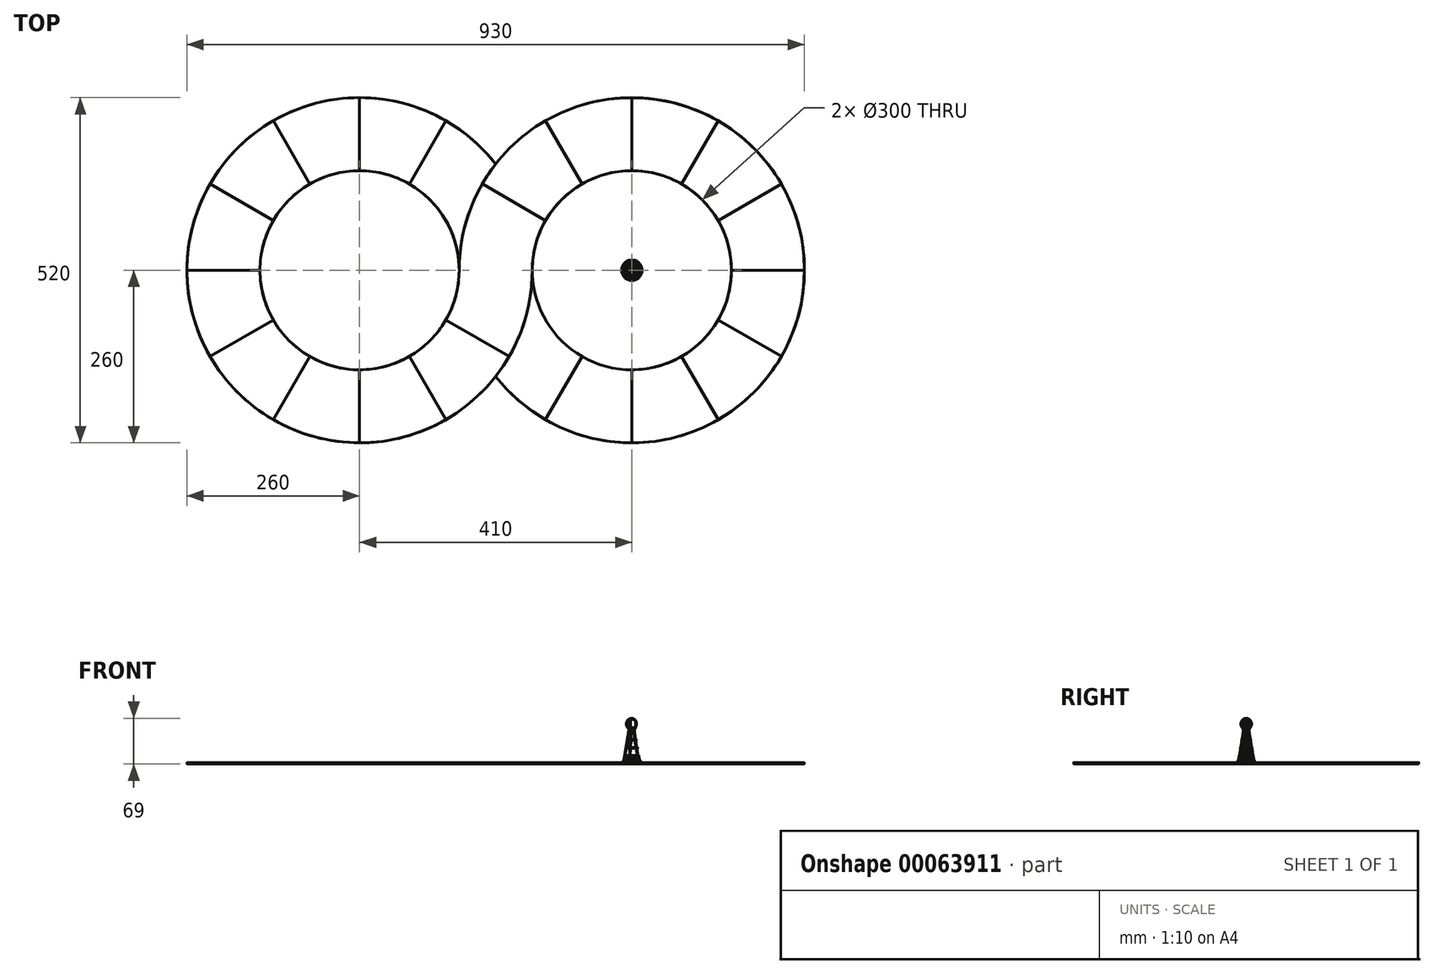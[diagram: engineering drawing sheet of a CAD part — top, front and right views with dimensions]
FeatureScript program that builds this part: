
annotation { "Feature Type Name" : "Feature", "Feature Type Description" : "" }
export const myFeature = defineFeature(function(context is Context, id is Id, definition is map)
    precondition{}
    {
        {
            var Q0;
            Q0=qCreatedBy(makeId("Top.planeOp"),FACE);
            var sketch = newSketch(context, id + "F0", { "sketchPlane" : qUnion([Q0])});
            skArc(sketch, "E0", {"start": v(-205, -159.92) * mm, "mid": v(245.87, 84.56) * mm, "end": v(-260, 0) * mm});
            skArc(sketch, "E1", {"start": v(-205, 159.92) * mm, "mid": v(-655.87, -84.56) * mm, "end": v(-150, 0) * mm});
            skCircle(sketch, "E2", {"center": v(-410, 0) * mm, "radius": 150 * mm});
            skCircle(sketch, "E3", {"center": v(0, 0) * mm, "radius": 150 * mm});
            skLineSegment(sketch, "E4.9.0", {"start": v(-260, 0) * mm, "end": v(-150, 0) * mm});
            skLineSegment(sketch, "E5.2.0", {"start": v(-130, -225.17) * mm, "end": v(-75, -129.9) * mm});
            skLineSegment(sketch, "E5.3.0", {"start": v(0, -260) * mm, "end": v(0, -150) * mm});
            skLineSegment(sketch, "E5.4.0", {"start": v(130, -225.17) * mm, "end": v(75, -129.9) * mm});
            skLineSegment(sketch, "E5.5.0", {"start": v(225.17, -130) * mm, "end": v(129.9, -75) * mm});
            skLineSegment(sketch, "E5.6.0", {"start": v(260, 0) * mm, "end": v(150, 0) * mm});
            skLineSegment(sketch, "E5.7.0", {"start": v(225.17, 130) * mm, "end": v(129.9, 75) * mm});
            skLineSegment(sketch, "E5.8.0", {"start": v(130, 225.17) * mm, "end": v(75, 129.9) * mm});
            skLineSegment(sketch, "E5.9.0", {"start": v(0, 260) * mm, "end": v(0, 150) * mm});
            skLineSegment(sketch, "E5.10.0", {"start": v(-130, 225.17) * mm, "end": v(-75, 129.9) * mm});
            skLineSegment(sketch, "E5.11.0", {"start": v(-225.17, 130) * mm, "end": v(-129.9, 75) * mm});
            skSolve(sketch);
        }
        {
            var Q0;
            Q0=qCreatedBy(makeId("Top.planeOp"),FACE);
            var sketch = newSketch(context, id + "F1", { "sketchPlane" : qUnion([Q0])});
            skLineSegment(sketch, "E6", {"start": v(-670, 0) * mm, "end": v(-560, 0) * mm});
            skCircle(sketch, "E7", {"center": v(-410, 0) * mm, "radius": 150 * mm, "construction": true});
            skLineSegment(sketch, "E8.1.0", {"start": v(-635.17, -130) * mm, "end": v(-539.9, -75) * mm});
            skLineSegment(sketch, "E8.2.0", {"start": v(-540, -225.17) * mm, "end": v(-485, -129.9) * mm});
            skLineSegment(sketch, "E8.3.0", {"start": v(-410, -260) * mm, "end": v(-410, -150) * mm});
            skLineSegment(sketch, "E8.4.0", {"start": v(-280, -225.17) * mm, "end": v(-335, -129.9) * mm});
            skLineSegment(sketch, "E8.5.0", {"start": v(-184.83, -130) * mm, "end": v(-280.1, -75) * mm});
            skLineSegment(sketch, "E8.8.0", {"start": v(-280, 225.17) * mm, "end": v(-335, 129.9) * mm});
            skLineSegment(sketch, "E8.9.0", {"start": v(-410, 260) * mm, "end": v(-410, 150) * mm});
            skLineSegment(sketch, "E8.10.0", {"start": v(-540, 225.17) * mm, "end": v(-485, 129.9) * mm});
            skLineSegment(sketch, "E8.11.0", {"start": v(-635.17, 130) * mm, "end": v(-539.9, 75) * mm});
            skCircle(sketch, "E9", {"center": v(-410, 0) * mm, "radius": 150 * mm});
            skCircle(sketch, "E10", {"center": v(-410, 0) * mm, "radius": 260 * mm});
            skLineSegment(sketch, "E11", {"start": v(-260, 0) * mm, "end": v(-150, 0) * mm});
            skSolve(sketch);
        }
        {
            var Q0;
            {var subQ3=sQuery(id+"F0.wireOp",EDGE,"E5.2.0");Q0=makeQuery(id+"F0.imprint","IMPRINT",FACE,{"disambiguationData":[TD([[makeQuery(id+"F0.imprint","IMPRINT",EDGE,{"derivedFrom":subQ3}),1.0]])]});}
            extrude(context, id + "F2", {"entities" : qUnion([Q0]), "depth" : 1 * mm});
        }
        {
            var Q0;
            {var subQ0=sQuery(id+"F0.wireOp",EDGE,"E5.2.0");Q0=makeQuery(id+"F0.imprint","IMPRINT",FACE,{"disambiguationData":[TD([[makeQuery(id+"F0.imprint","IMPRINT",EDGE,{"derivedFrom":subQ0}),-1.0]])]});}
            extrude(context, id + "F3", {"entities" : qUnion([Q0]), "operationType" : NewBodyOperationType.ADD, "depth" : 1.1 * mm});
        }
        {
            var Q0;
            {var subQ0=sQuery(id+"F0.wireOp",EDGE,"E5.3.0");Q0=makeQuery(id+"F0.imprint","IMPRINT",FACE,{"disambiguationData":[TD([[makeQuery(id+"F0.imprint","IMPRINT",EDGE,{"derivedFrom":subQ0}),-1.0]])]});}
            extrude(context, id + "F4", {"entities" : qUnion([Q0]), "operationType" : NewBodyOperationType.ADD, "depth" : 1.2 * mm});
        }
        {
            var Q0;
            {var subQ0=sQuery(id+"F0.wireOp",EDGE,"E5.4.0");Q0=makeQuery(id+"F0.imprint","IMPRINT",FACE,{"disambiguationData":[TD([[makeQuery(id+"F0.imprint","IMPRINT",EDGE,{"derivedFrom":subQ0}),-1.0]])]});}
            extrude(context, id + "F5", {"entities" : qUnion([Q0]), "operationType" : NewBodyOperationType.ADD, "depth" : 1.3 * mm});
        }
        {
            var Q0;
            {var subQ0=sQuery(id+"F0.wireOp",EDGE,"E5.5.0");Q0=makeQuery(id+"F0.imprint","IMPRINT",FACE,{"disambiguationData":[TD([[makeQuery(id+"F0.imprint","IMPRINT",EDGE,{"derivedFrom":subQ0}),-1.0]])]});}
            extrude(context, id + "F6", {"entities" : qUnion([Q0]), "operationType" : NewBodyOperationType.ADD, "depth" : 1.4 * mm});
        }
        {
            var Q0;
            {var subQ0=sQuery(id+"F0.wireOp",EDGE,"E5.6.0");Q0=makeQuery(id+"F0.imprint","IMPRINT",FACE,{"disambiguationData":[TD([[makeQuery(id+"F0.imprint","IMPRINT",EDGE,{"derivedFrom":subQ0}),-1.0]])]});}
            extrude(context, id + "F7", {"entities" : qUnion([Q0]), "operationType" : NewBodyOperationType.ADD, "depth" : 1.5 * mm});
        }
        {
            var Q0;
            {var subQ0=sQuery(id+"F0.wireOp",EDGE,"E5.7.0");Q0=makeQuery(id+"F0.imprint","IMPRINT",FACE,{"disambiguationData":[TD([[makeQuery(id+"F0.imprint","IMPRINT",EDGE,{"derivedFrom":subQ0}),-1.0]])]});}
            extrude(context, id + "F8", {"entities" : qUnion([Q0]), "operationType" : NewBodyOperationType.ADD, "depth" : 1.6 * mm});
        }
        {
            var Q0;
            {var subQ0=sQuery(id+"F0.wireOp",EDGE,"E5.8.0");Q0=makeQuery(id+"F0.imprint","IMPRINT",FACE,{"disambiguationData":[TD([[makeQuery(id+"F0.imprint","IMPRINT",EDGE,{"derivedFrom":subQ0}),-1.0]])]});}
            extrude(context, id + "F9", {"entities" : qUnion([Q0]), "operationType" : NewBodyOperationType.ADD, "depth" : 1.7 * mm});
        }
        {
            var Q0;
            {var subQ0=sQuery(id+"F0.wireOp",EDGE,"E5.9.0");Q0=makeQuery(id+"F0.imprint","IMPRINT",FACE,{"disambiguationData":[TD([[makeQuery(id+"F0.imprint","IMPRINT",EDGE,{"derivedFrom":subQ0}),-1.0]])]});}
            extrude(context, id + "F10", {"entities" : qUnion([Q0]), "operationType" : NewBodyOperationType.ADD, "depth" : 1.8 * mm});
        }
        {
            var Q0;
            {var subQ0=sQuery(id+"F0.wireOp",EDGE,"E5.10.0");Q0=makeQuery(id+"F0.imprint","IMPRINT",FACE,{"disambiguationData":[TD([[makeQuery(id+"F0.imprint","IMPRINT",EDGE,{"derivedFrom":subQ0}),-1.0]])]});}
            extrude(context, id + "F11", {"entities" : qUnion([Q0]), "operationType" : NewBodyOperationType.ADD, "depth" : 1.9 * mm});
        }
        {
            var Q0;
            Q0=qCreatedBy(makeId("Top.planeOp"),FACE);
            var sketch = newSketch(context, id + "F12", { "sketchPlane" : qUnion([Q0])});
            skLineSegment(sketch, "E12", {"start": v(-260, 0) * mm, "end": v(-150, 0) * mm});
            skLineSegment(sketch, "E13", {"start": v(-225.17, 130) * mm, "end": v(-129.9, 75) * mm});
            skArc(sketch, "E14", {"start": v(-225.17, 130) * mm, "mid": v(-251.14, 67.3) * mm, "end": v(-260, 0) * mm});
            skArc(sketch, "E15", {"start": v(-129.9, 75) * mm, "mid": v(-144.89, 38.82) * mm, "end": v(-150, 0) * mm});
            skSolve(sketch);
        }
        {
            var Q0;
            {var subQ0=sQuery(id+"F1.wireOp",EDGE,"E8.5.0");Q0=makeQuery(id+"F1.imprint","IMPRINT",FACE,{"disambiguationData":[TD([[makeQuery(id+"F1.imprint","IMPRINT",EDGE,{"derivedFrom":subQ0}),-1.0]])]});}
            extrude(context, id + "F13", {"entities" : qUnion([Q0]), "operationType" : NewBodyOperationType.ADD, "depth" : 2 * mm});
        }
        {
            var Q0;
            {var subQ0=sQuery(id+"F1.wireOp",EDGE,"E8.4.0");Q0=makeQuery(id+"F1.imprint","IMPRINT",FACE,{"disambiguationData":[TD([[makeQuery(id+"F1.imprint","IMPRINT",EDGE,{"derivedFrom":subQ0}),-1.0]])]});}
            extrude(context, id + "F14", {"entities" : qUnion([Q0]), "operationType" : NewBodyOperationType.ADD, "depth" : 1.9 * mm});
        }
        {
            var Q0;
            {var subQ0=sQuery(id+"F1.wireOp",EDGE,"E8.3.0");Q0=makeQuery(id+"F1.imprint","IMPRINT",FACE,{"disambiguationData":[TD([[makeQuery(id+"F1.imprint","IMPRINT",EDGE,{"derivedFrom":subQ0}),-1.0]])]});}
            extrude(context, id + "F15", {"entities" : qUnion([Q0]), "operationType" : NewBodyOperationType.ADD, "depth" : 1.8 * mm});
        }
        {
            var Q0;
            {var subQ0=sQuery(id+"F1.wireOp",EDGE,"E8.2.0");Q0=makeQuery(id+"F1.imprint","IMPRINT",FACE,{"disambiguationData":[TD([[makeQuery(id+"F1.imprint","IMPRINT",EDGE,{"derivedFrom":subQ0}),-1.0]])]});}
            extrude(context, id + "F16", {"entities" : qUnion([Q0]), "operationType" : NewBodyOperationType.ADD, "depth" : 1.7 * mm});
        }
        {
            var Q0;
            {var subQ0=sQuery(id+"F1.wireOp",EDGE,"E8.8.0");Q0=makeQuery(id+"F1.imprint","IMPRINT",FACE,{"disambiguationData":[TD([[makeQuery(id+"F1.imprint","IMPRINT",EDGE,{"derivedFrom":subQ0}),1.0]])]});}
            extrude(context, id + "F17", {"entities" : qUnion([Q0]), "operationType" : NewBodyOperationType.ADD, "depth" : 1 * mm});
        }
        {
            var Q0;
            Q0=makeQuery(id+"F12.imprint","IMPRINT",FACE,{"disambiguationData":[TD([[makeQuery(id+"F12.imprint","IMPRINT",EDGE,{"derivedFrom":sQuery(id+"F12.wireOp",EDGE,"E12")}),1.0]])]});
            extrude(context, id + "F18", {"entities" : qUnion([Q0]), "operationType" : NewBodyOperationType.ADD, "depth" : 2 * mm});
        }
        {
            var Q0;
            {var subQ0=sQuery(id+"F1.wireOp",EDGE,"E8.8.0");Q0=makeQuery(id+"F1.imprint","IMPRINT",FACE,{"disambiguationData":[TD([[makeQuery(id+"F1.imprint","IMPRINT",EDGE,{"derivedFrom":subQ0}),-1.0]])]});}
            extrude(context, id + "F19", {"entities" : qUnion([Q0]), "operationType" : NewBodyOperationType.ADD, "depth" : 1.1 * mm});
        }
        {
            var Q0;
            {var subQ0=sQuery(id+"F1.wireOp",EDGE,"E8.9.0");Q0=makeQuery(id+"F1.imprint","IMPRINT",FACE,{"disambiguationData":[TD([[makeQuery(id+"F1.imprint","IMPRINT",EDGE,{"derivedFrom":subQ0}),-1.0]])]});}
            extrude(context, id + "F20", {"entities" : qUnion([Q0]), "operationType" : NewBodyOperationType.ADD, "depth" : 1.2 * mm});
        }
        {
            var Q0;
            {var subQ0=sQuery(id+"F1.wireOp",EDGE,"E8.10.0");Q0=makeQuery(id+"F1.imprint","IMPRINT",FACE,{"disambiguationData":[TD([[makeQuery(id+"F1.imprint","IMPRINT",EDGE,{"derivedFrom":subQ0}),-1.0]])]});}
            extrude(context, id + "F21", {"entities" : qUnion([Q0]), "operationType" : NewBodyOperationType.ADD, "depth" : 1.3 * mm});
        }
        {
            var Q0;
            {var subQ0=sQuery(id+"F1.wireOp",EDGE,"E6");Q0=makeQuery(id+"F1.imprint","IMPRINT",FACE,{"disambiguationData":[TD([[makeQuery(id+"F1.imprint","IMPRINT",EDGE,{"derivedFrom":subQ0}),1.0]])]});}
            extrude(context, id + "F22", {"entities" : qUnion([Q0]), "operationType" : NewBodyOperationType.ADD, "depth" : 1.4 * mm});
        }
        {
            var Q0;
            {var subQ0=sQuery(id+"F1.wireOp",EDGE,"E6");Q0=makeQuery(id+"F1.imprint","IMPRINT",FACE,{"disambiguationData":[TD([[makeQuery(id+"F1.imprint","IMPRINT",EDGE,{"derivedFrom":subQ0}),-1.0]])]});}
            extrude(context, id + "F23", {"entities" : qUnion([Q0]), "operationType" : NewBodyOperationType.ADD, "depth" : 1.5 * mm});
        }
        {
            var Q0;
            {var subQ0=sQuery(id+"F1.wireOp",EDGE,"E8.1.0");Q0=makeQuery(id+"F1.imprint","IMPRINT",FACE,{"disambiguationData":[TD([[makeQuery(id+"F1.imprint","IMPRINT",EDGE,{"derivedFrom":subQ0}),-1.0]])]});}
            extrude(context, id + "F24", {"entities" : qUnion([Q0]), "operationType" : NewBodyOperationType.ADD, "depth" : 1.6 * mm});
        }
        {
            var Q0;
            {var subQ0=sQuery(id+"F0.wireOp",EDGE,"E3");Q0=makeQuery(id+"F18.boolean.opBoolean","MERGE",FACE,{"derivedFrom":[makeQuery(id+"F11.boolean.opBoolean","MERGE",FACE,{"derivedFrom":[makeQuery(id+"F10.boolean.opBoolean","MERGE",FACE,{"derivedFrom":[makeQuery(id+"F9.boolean.opBoolean","MERGE",FACE,{"derivedFrom":[makeQuery(id+"F8.boolean.opBoolean","MERGE",FACE,{"derivedFrom":[makeQuery(id+"F7.boolean.opBoolean","MERGE",FACE,{"derivedFrom":[makeQuery(id+"F6.boolean.opBoolean","MERGE",FACE,{"derivedFrom":[makeQuery(id+"F5.boolean.opBoolean","MERGE",FACE,{"derivedFrom":[makeQuery(id+"F4.boolean.opBoolean","MERGE",FACE,{"derivedFrom":[makeQuery(id+"F3.boolean.opBoolean","MERGE",FACE,{"derivedFrom":[makeQuery(id+"F2.opExtrude","SWEPT_FACE",FACE,{"disambiguationData":[OSD([subQ0])]}),makeQuery(id+"F3.opExtrude","SWEPT_FACE",FACE,{"disambiguationData":[OSD([subQ0])]})]}),makeQuery(id+"F4.opExtrude","SWEPT_FACE",FACE,{"disambiguationData":[OSD([subQ0])]})]}),makeQuery(id+"F5.opExtrude","SWEPT_FACE",FACE,{"disambiguationData":[OSD([subQ0])]})]}),makeQuery(id+"F6.opExtrude","SWEPT_FACE",FACE,{"disambiguationData":[OSD([subQ0])]})]}),makeQuery(id+"F7.opExtrude","SWEPT_FACE",FACE,{"disambiguationData":[OSD([subQ0])]})]}),makeQuery(id+"F8.opExtrude","SWEPT_FACE",FACE,{"disambiguationData":[OSD([subQ0])]})]}),makeQuery(id+"F9.opExtrude","SWEPT_FACE",FACE,{"disambiguationData":[OSD([subQ0])]})]}),makeQuery(id+"F10.opExtrude","SWEPT_FACE",FACE,{"disambiguationData":[OSD([subQ0])]})]}),makeQuery(id+"F11.opExtrude","SWEPT_FACE",FACE,{"disambiguationData":[OSD([subQ0])]})]}),makeQuery(id+"F18.opExtrude","SWEPT_FACE",FACE,{"disambiguationData":[OSD([sQuery(id+"F12.wireOp",EDGE,"E15")])]})]});}
            var Q1;
            {var subQ0=sQuery(id+"F1.wireOp",EDGE,"E9");Q1=makeQuery(id+"F24.boolean.opBoolean","MERGE",FACE,{"derivedFrom":[makeQuery(id+"F23.boolean.opBoolean","MERGE",FACE,{"derivedFrom":[makeQuery(id+"F22.boolean.opBoolean","MERGE",FACE,{"derivedFrom":[makeQuery(id+"F21.boolean.opBoolean","MERGE",FACE,{"derivedFrom":[makeQuery(id+"F20.boolean.opBoolean","MERGE",FACE,{"derivedFrom":[makeQuery(id+"F19.boolean.opBoolean","MERGE",FACE,{"derivedFrom":[makeQuery(id+"F17.boolean.opBoolean","MERGE",FACE,{"derivedFrom":[makeQuery(id+"F16.boolean.opBoolean","MERGE",FACE,{"derivedFrom":[makeQuery(id+"F15.boolean.opBoolean","MERGE",FACE,{"derivedFrom":[makeQuery(id+"F14.boolean.opBoolean","MERGE",FACE,{"derivedFrom":[makeQuery(id+"F13.opExtrude","SWEPT_FACE",FACE,{"disambiguationData":[OSD([subQ0])]}),makeQuery(id+"F14.opExtrude","SWEPT_FACE",FACE,{"disambiguationData":[OSD([subQ0])]})]}),makeQuery(id+"F15.opExtrude","SWEPT_FACE",FACE,{"disambiguationData":[OSD([subQ0])]})]}),makeQuery(id+"F16.opExtrude","SWEPT_FACE",FACE,{"disambiguationData":[OSD([subQ0])]})]}),makeQuery(id+"F17.opExtrude","SWEPT_FACE",FACE,{"disambiguationData":[OSD([subQ0])]})]}),makeQuery(id+"F19.opExtrude","SWEPT_FACE",FACE,{"disambiguationData":[OSD([subQ0])]})]}),makeQuery(id+"F20.opExtrude","SWEPT_FACE",FACE,{"disambiguationData":[OSD([subQ0])]})]}),makeQuery(id+"F21.opExtrude","SWEPT_FACE",FACE,{"disambiguationData":[OSD([subQ0])]})]}),makeQuery(id+"F22.opExtrude","SWEPT_FACE",FACE,{"disambiguationData":[OSD([subQ0])]})]}),makeQuery(id+"F23.opExtrude","SWEPT_FACE",FACE,{"disambiguationData":[OSD([subQ0])]})]}),makeQuery(id+"F24.opExtrude","SWEPT_FACE",FACE,{"disambiguationData":[OSD([subQ0])]})]});}
            var Q2;
            {var subQ0=sQuery(id+"F1.wireOp",EDGE,"E10");var subQ1=sQuery(id+"F0.wireOp",EDGE,"E0");Q2=makeQuery(id+"F24.boolean.opBoolean","MERGE",FACE,{"derivedFrom":[makeQuery(id+"F16.boolean.opBoolean","MERGE",FACE,{"derivedFrom":[makeQuery(id+"F15.boolean.opBoolean","MERGE",FACE,{"derivedFrom":[makeQuery(id+"F14.boolean.opBoolean","MERGE",FACE,{"derivedFrom":[makeQuery(id+"F13.opExtrude","SWEPT_FACE",FACE,{"disambiguationData":[OSD([subQ0])]}),makeQuery(id+"F14.opExtrude","SWEPT_FACE",FACE,{"disambiguationData":[OSD([subQ0])]})]}),makeQuery(id+"F15.opExtrude","SWEPT_FACE",FACE,{"disambiguationData":[OSD([subQ0])]})]}),makeQuery(id+"F16.opExtrude","SWEPT_FACE",FACE,{"disambiguationData":[OSD([subQ0])]})]}),makeQuery(id+"F23.boolean.opBoolean","MERGE",FACE,{"derivedFrom":[makeQuery(id+"F22.boolean.opBoolean","MERGE",FACE,{"derivedFrom":[makeQuery(id+"F21.boolean.opBoolean","MERGE",FACE,{"derivedFrom":[makeQuery(id+"F20.boolean.opBoolean","MERGE",FACE,{"derivedFrom":[makeQuery(id+"F19.boolean.opBoolean","MERGE",FACE,{"derivedFrom":[makeQuery(id+"F17.boolean.opBoolean","SPLIT",FACE,{"disambiguationData":[TD([makeQuery(id+"F2.opExtrude","SWEPT_FACE",FACE,{"disambiguationData":[OSD([subQ1])]})])],"derivedFrom":makeQuery(id+"F17.opExtrude","SWEPT_FACE",FACE,{"disambiguationData":[OSD([subQ0])]})}),makeQuery(id+"F19.opExtrude","SWEPT_FACE",FACE,{"disambiguationData":[OSD([subQ0])]})]}),makeQuery(id+"F20.opExtrude","SWEPT_FACE",FACE,{"disambiguationData":[OSD([subQ0])]})]}),makeQuery(id+"F21.opExtrude","SWEPT_FACE",FACE,{"disambiguationData":[OSD([subQ0])]})]}),makeQuery(id+"F22.opExtrude","SWEPT_FACE",FACE,{"disambiguationData":[OSD([subQ0])]})]}),makeQuery(id+"F23.opExtrude","SWEPT_FACE",FACE,{"disambiguationData":[OSD([subQ0])]})]}),makeQuery(id+"F24.opExtrude","SWEPT_FACE",FACE,{"disambiguationData":[OSD([subQ0])]})]});}
            var Q3;
            {var subQ0=sQuery(id+"F0.wireOp",EDGE,"E0");Q3=makeQuery(id+"F18.boolean.opBoolean","MERGE",FACE,{"derivedFrom":[makeQuery(id+"F11.boolean.opBoolean","MERGE",FACE,{"derivedFrom":[makeQuery(id+"F10.boolean.opBoolean","MERGE",FACE,{"derivedFrom":[makeQuery(id+"F9.boolean.opBoolean","MERGE",FACE,{"derivedFrom":[makeQuery(id+"F8.boolean.opBoolean","MERGE",FACE,{"derivedFrom":[makeQuery(id+"F7.boolean.opBoolean","MERGE",FACE,{"derivedFrom":[makeQuery(id+"F6.boolean.opBoolean","MERGE",FACE,{"derivedFrom":[makeQuery(id+"F5.boolean.opBoolean","MERGE",FACE,{"derivedFrom":[makeQuery(id+"F4.boolean.opBoolean","MERGE",FACE,{"derivedFrom":[makeQuery(id+"F3.boolean.opBoolean","MERGE",FACE,{"derivedFrom":[makeQuery(id+"F2.opExtrude","SWEPT_FACE",FACE,{"disambiguationData":[OSD([subQ0])]}),makeQuery(id+"F3.opExtrude","SWEPT_FACE",FACE,{"disambiguationData":[OSD([subQ0])]})]}),makeQuery(id+"F4.opExtrude","SWEPT_FACE",FACE,{"disambiguationData":[OSD([subQ0])]})]}),makeQuery(id+"F5.opExtrude","SWEPT_FACE",FACE,{"disambiguationData":[OSD([subQ0])]})]}),makeQuery(id+"F6.opExtrude","SWEPT_FACE",FACE,{"disambiguationData":[OSD([subQ0])]})]}),makeQuery(id+"F7.opExtrude","SWEPT_FACE",FACE,{"disambiguationData":[OSD([subQ0])]})]}),makeQuery(id+"F8.opExtrude","SWEPT_FACE",FACE,{"disambiguationData":[OSD([subQ0])]})]}),makeQuery(id+"F9.opExtrude","SWEPT_FACE",FACE,{"disambiguationData":[OSD([subQ0])]})]}),makeQuery(id+"F10.opExtrude","SWEPT_FACE",FACE,{"disambiguationData":[OSD([subQ0])]})]}),makeQuery(id+"F11.opExtrude","SWEPT_FACE",FACE,{"disambiguationData":[OSD([subQ0])]})]}),makeQuery(id+"F18.opExtrude","SWEPT_FACE",FACE,{"disambiguationData":[OSD([sQuery(id+"F12.wireOp",EDGE,"E14")])]})]});}
            fillet(context, id + "F25", {"entities" : qUnion([Q0, Q1, Q2, Q3]), "radius" : 0.1 * mm, "tangentPropagation" : true, "allowEdgeOverflow" : false});
        }
        {
            var Q0;
            Q0=qCreatedBy(makeId("Top.planeOp"),FACE);
            var sketch = newSketch(context, id + "F26", { "sketchPlane" : qUnion([Q0])});
            skCircle(sketch, "E16", {"center": v(0, 0) * mm, "radius": 15 * mm});
            skCircle(sketch, "E17", {"center": v(0, 0) * mm, "radius": 10 * mm});
            skSolve(sketch);
        }
        {
            var Q0;
            Q0=qCreatedBy(makeId("Front.planeOp"),FACE);
            var sketch = newSketch(context, id + "F27", { "sketchPlane" : qUnion([Q0])});
            skCircle(sketch, "E18", {"center": v(-15, 0) * mm, "radius": 0.5 * mm});
            skLineSegment(sketch, "E19.0", {"start": v(-14.13, 0) * mm, "end": v(-10, 0) * mm});
            skLineSegment(sketch, "E20.0", {"start": v(-10, 0) * mm, "end": v(10, 0) * mm});
            skCircle(sketch, "E21", {"center": v(-10, 0) * mm, "radius": 0.5 * mm});
            skLineSegment(sketch, "E22.0", {"start": v(-8.27, 2) * mm, "end": v(0, 2) * mm});
            skLineSegment(sketch, "E23", {"start": v(-9.57, 0.25) * mm, "end": v(-8.7, 1.75) * mm});
            skLineSegment(sketch, "E24", {"start": v(0, 0) * mm, "end": v(0, 60) * mm});
            skLineSegment(sketch, "E25", {"start": v(-14.57, 0.75) * mm, "end": v(-11.58, 5.92) * mm});
            skLineSegment(sketch, "E26", {"start": v(-11.52, 6.09) * mm, "end": v(-4, 49.7) * mm});
            skArc(sketch, "E27", {"start": v(-5.5, 54.18) * mm, "mid": v(-7.43, 62.96) * mm, "end": v(0, 68) * mm});
            skPoint(sketch, "E28.visualSharp", {"position": v(-3.47, 52.8) * mm});
            skArc(sketch, "E28.filletArc", {"start": v(-4, 49.7) * mm, "mid": v(-4.18, 52.13) * mm, "end": v(-5.5, 54.18) * mm});
            skLineSegment(sketch, "E29.0.1.0", {"start": v(-10, 12) * mm, "end": v(0, 12) * mm});
            skLineSegment(sketch, "E29.0.2.0", {"start": v(-8.43, 24) * mm, "end": v(0, 24) * mm});
            skLineSegment(sketch, "E29.0.3.0", {"start": v(-6.36, 36) * mm, "end": v(0, 36) * mm});
            skLineSegment(sketch, "E29.0.4.0", {"start": v(-4, 49.7) * mm, "end": v(0, 49.7) * mm});
            skLineSegment(sketch, "E29.direction1", {"start": v(-10, 0) * mm, "end": v(15, 0) * mm, "construction": true});
            skLineSegment(sketch, "E29.direction2", {"start": v(-10, 0) * mm, "end": v(-10, 12) * mm, "construction": true});
            skLineSegment(sketch, "E30", {"start": v(-11.54, 6) * mm, "end": v(-25.34, 6) * mm, "construction": true});
            skLineSegment(sketch, "E31", {"start": v(-10, 12) * mm, "end": v(-10.5, 12) * mm});
            skCircle(sketch, "E32", {"center": v(-11.54, 6) * mm, "radius": 0.5 * mm});
            skCircle(sketch, "E33", {"center": v(-10.5, 12) * mm, "radius": 0.5 * mm});
            skCircle(sketch, "E34", {"center": v(-8.43, 24) * mm, "radius": 0.5 * mm});
            skCircle(sketch, "E35", {"center": v(-6.36, 36) * mm, "radius": 0.5 * mm});
            skCircle(sketch, "E36", {"center": v(-4, 49.7) * mm, "radius": 0.5 * mm});
            skCircle(sketch, "E37", {"center": v(-5.5, 54.18) * mm, "radius": 0.5 * mm});
            skCircle(sketch, "E38", {"center": v(-8.56, 2) * mm, "radius": 0.5 * mm});
            skCircle(sketch, "E39", {"center": v(-4.28, 2) * mm, "radius": 0.5 * mm});
            skArc(sketch, "E40.filletArc", {"start": v(-8.27, 2) * mm, "mid": v(-8.52, 1.93) * mm, "end": v(-8.7, 1.75) * mm});
            skPoint(sketch, "E41.newPointA", {"position": v(15, 0) * mm});
            skArc(sketch, "E41.filletArc", {"start": v(-10, 0) * mm, "mid": v(-9.75, 0.07) * mm, "end": v(-9.57, 0.25) * mm});
            skArc(sketch, "E42.filletArc", {"start": v(-14.57, 0.75) * mm, "mid": v(-14.57, 0.25) * mm, "end": v(-14.13, 0) * mm});
            skArc(sketch, "E43.filletArc", {"start": v(-11.58, 5.92) * mm, "mid": v(-11.54, 6) * mm, "end": v(-11.52, 6.09) * mm});
            skSolve(sketch);
        }
        {
            var Q0;
            Q0=qCreatedBy(makeId("Right.planeOp"),FACE);
            var sketch = newSketch(context, id + "F28", { "sketchPlane" : qUnion([Q0])});
            skCircle(sketch, "E44", {"center": v(0, 68) * mm, "radius": 0.5 * mm});
            skSolve(sketch);
        }
        {
            var Q0;
            Q0=makeQuery(id+"F28.imprint","IMPRINT",FACE,{"disambiguationData":[TD([[makeQuery(id+"F28.imprint","IMPRINT",EDGE,{"derivedFrom":sQuery(id+"F28.wireOp",EDGE,"E44")}),1.0]])]});
            var Q1;
            Q1=sQuery(id+"F28.wireOp",EDGE,"E44");
            var Q2;
            Q2=sQuery(id+"F27.wireOp",EDGE,"E27");
            var Q3;
            Q3=sQuery(id+"F27.wireOp",EDGE,"E28.filletArc");
            var Q4;
            Q4=sQuery(id+"F27.wireOp",EDGE,"E26");
            var Q5;
            Q5=sQuery(id+"F27.wireOp",EDGE,"E43.filletArc");
            var Q6;
            Q6=sQuery(id+"F27.wireOp",EDGE,"E25");
            var Q7;
            Q7=sQuery(id+"F27.wireOp",EDGE,"E42.filletArc");
            var Q8;
            Q8=sQuery(id+"F27.wireOp",EDGE,"E19.0");
            var Q9;
            Q9=sQuery(id+"F27.wireOp",EDGE,"E41.filletArc");
            var Q10;
            Q10=sQuery(id+"F27.wireOp",EDGE,"E23");
            var Q11;
            Q11=sQuery(id+"F27.wireOp",EDGE,"E40.filletArc");
            var Q12;
            Q12=sQuery(id+"F27.wireOp",EDGE,"E22.0");
            sweep(context, id + "F29", {"profiles" : qUnion([Q0]), "surfaceProfiles" : qUnion([Q1]), "path" : qUnion([Q2, Q3, Q4, Q5, Q6, Q7, Q8, Q9, Q10, Q11, Q12])});
        }
        {
            var Q0;
            Q0=makeQuery(id+"F27.imprint","IMPRINT",FACE,{"disambiguationData":[TD([[makeQuery(id+"F27.imprint","IMPRINT",EDGE,{"derivedFrom":sQuery(id+"F27.wireOp",EDGE,"E18")}),1.0]])]});
            var Q1;
            Q1=sQuery(id+"F26.wireOp",EDGE,"E16");
            sweep(context, id + "F30", {"profiles" : qUnion([Q0]), "path" : qUnion([Q1])});
        }
        {
            var Q0;
            {var subQ0=sQuery(id+"F27.wireOp",EDGE,"E26");var subQ1=sQuery(id+"F27.wireOp",EDGE,"E25");var subQ2=makeQuery(id+"F27.imprint","INTERSECT",VERTEX,{"derivedFrom":[subQ1,subQ0]});Q0=makeQuery(id+"F27.imprint","IMPRINT",FACE,{"disambiguationData":[TD([[makeQuery(id+"F27.imprint","IMPRINT",EDGE,{"disambiguationData":[TD([[subQ2,1.0]])],"derivedFrom":subQ1}),1.0]])]});}
            var Q1;
            {var subQ0=sQuery(id+"F27.wireOp",EDGE,"E26");var subQ1=sQuery(id+"F27.wireOp",EDGE,"E25");var subQ2=makeQuery(id+"F27.imprint","INTERSECT",VERTEX,{"derivedFrom":[subQ1,subQ0]});Q1=makeQuery(id+"F27.imprint","IMPRINT",FACE,{"disambiguationData":[TD([[makeQuery(id+"F27.imprint","IMPRINT",EDGE,{"disambiguationData":[TD([[subQ2,1.0]])],"derivedFrom":subQ1}),-1.0]])]});}
            var Q2;
            {var subQ0=sQuery(id+"F27.wireOp",EDGE,"E31");var subQ1=sQuery(id+"F27.wireOp",EDGE,"E26");var subQ2=makeQuery(id+"F27.imprint","INTERSECT",VERTEX,{"derivedFrom":[subQ1,subQ0]});Q2=makeQuery(id+"F27.imprint","IMPRINT",FACE,{"disambiguationData":[TD([[makeQuery(id+"F27.imprint","IMPRINT",EDGE,{"disambiguationData":[TD([[subQ2,1.0]])],"derivedFrom":subQ1}),-1.0]])]});}
            var Q3;
            {var subQ0=sQuery(id+"F27.wireOp",EDGE,"E31");var subQ1=sQuery(id+"F27.wireOp",EDGE,"E26");var subQ2=makeQuery(id+"F27.imprint","INTERSECT",VERTEX,{"derivedFrom":[subQ1,subQ0]});Q3=makeQuery(id+"F27.imprint","IMPRINT",FACE,{"disambiguationData":[TD([[makeQuery(id+"F27.imprint","IMPRINT",EDGE,{"disambiguationData":[TD([[subQ2,-1.0]])],"derivedFrom":subQ1}),-1.0]])]});}
            var Q4;
            {var subQ0=sQuery(id+"F27.wireOp",EDGE,"E26");var subQ1=makeQuery(id+"F27.imprint","INTERSECT",VERTEX,{"derivedFrom":[subQ0,sQuery(id+"F27.wireOp",EDGE,"E31")]});Q4=makeQuery(id+"F27.imprint","IMPRINT",FACE,{"disambiguationData":[TD([[makeQuery(id+"F27.imprint","IMPRINT",EDGE,{"disambiguationData":[TD([[subQ1,1.0]])],"derivedFrom":subQ0}),1.0]])]});}
            var Q5;
            {var subQ0=sQuery(id+"F27.wireOp",EDGE,"E26");var subQ1=makeQuery(id+"F27.imprint","INTERSECT",VERTEX,{"derivedFrom":[subQ0,sQuery(id+"F27.wireOp",EDGE,"E29.0.2.0")]});Q5=makeQuery(id+"F27.imprint","IMPRINT",FACE,{"disambiguationData":[TD([[makeQuery(id+"F27.imprint","IMPRINT",EDGE,{"disambiguationData":[TD([[subQ1,1.0]])],"derivedFrom":subQ0}),1.0]])]});}
            var Q6;
            {var subQ0=sQuery(id+"F27.wireOp",EDGE,"E29.0.2.0");var subQ1=sQuery(id+"F27.wireOp",EDGE,"E26");var subQ2=makeQuery(id+"F27.imprint","INTERSECT",VERTEX,{"derivedFrom":[subQ1,subQ0]});Q6=makeQuery(id+"F27.imprint","IMPRINT",FACE,{"disambiguationData":[TD([[makeQuery(id+"F27.imprint","IMPRINT",EDGE,{"disambiguationData":[TD([[subQ2,1.0]])],"derivedFrom":subQ1}),-1.0]])]});}
            var Q7;
            {var subQ0=sQuery(id+"F27.wireOp",EDGE,"E29.0.2.0");var subQ1=sQuery(id+"F27.wireOp",EDGE,"E26");var subQ2=makeQuery(id+"F27.imprint","INTERSECT",VERTEX,{"derivedFrom":[subQ1,subQ0]});Q7=makeQuery(id+"F27.imprint","IMPRINT",FACE,{"disambiguationData":[TD([[makeQuery(id+"F27.imprint","IMPRINT",EDGE,{"disambiguationData":[TD([[subQ2,-1.0]])],"derivedFrom":subQ1}),-1.0]])]});}
            var Q8;
            {var subQ0=sQuery(id+"F27.wireOp",EDGE,"E26");var subQ1=makeQuery(id+"F27.imprint","INTERSECT",VERTEX,{"derivedFrom":[subQ0,sQuery(id+"F27.wireOp",EDGE,"E29.0.3.0")]});Q8=makeQuery(id+"F27.imprint","IMPRINT",FACE,{"disambiguationData":[TD([[makeQuery(id+"F27.imprint","IMPRINT",EDGE,{"disambiguationData":[TD([[subQ1,1.0]])],"derivedFrom":subQ0}),1.0]])]});}
            var Q9;
            {var subQ0=sQuery(id+"F27.wireOp",EDGE,"E29.0.3.0");var subQ1=sQuery(id+"F27.wireOp",EDGE,"E26");var subQ2=makeQuery(id+"F27.imprint","INTERSECT",VERTEX,{"derivedFrom":[subQ1,subQ0]});Q9=makeQuery(id+"F27.imprint","IMPRINT",FACE,{"disambiguationData":[TD([[makeQuery(id+"F27.imprint","IMPRINT",EDGE,{"disambiguationData":[TD([[subQ2,-1.0]])],"derivedFrom":subQ1}),-1.0]])]});}
            var Q10;
            {var subQ0=sQuery(id+"F27.wireOp",EDGE,"E29.0.3.0");var subQ1=sQuery(id+"F27.wireOp",EDGE,"E26");var subQ2=makeQuery(id+"F27.imprint","INTERSECT",VERTEX,{"derivedFrom":[subQ1,subQ0]});Q10=makeQuery(id+"F27.imprint","IMPRINT",FACE,{"disambiguationData":[TD([[makeQuery(id+"F27.imprint","IMPRINT",EDGE,{"disambiguationData":[TD([[subQ2,1.0]])],"derivedFrom":subQ1}),-1.0]])]});}
            var Q11;
            {var subQ1=sQuery(id+"F27.wireOp",EDGE,"E26");var subQ3=sQuery(id+"F27.wireOp",EDGE,"E36");var subQ4=makeQuery(id+"F27.imprint","INTERSECT",VERTEX,{"derivedFrom":[subQ1,subQ3]});Q11=makeQuery(id+"F27.imprint","IMPRINT",FACE,{"disambiguationData":[TD([[makeQuery(id+"F27.imprint","IMPRINT",EDGE,{"disambiguationData":[TD([[subQ4,-1.0]])],"derivedFrom":subQ3}),1.0]])]});}
            var Q12;
            {var subQ1=sQuery(id+"F27.wireOp",EDGE,"E28.filletArc");var subQ3=sQuery(id+"F27.wireOp",EDGE,"E36");var subQ4=makeQuery(id+"F27.imprint","INTERSECT",VERTEX,{"derivedFrom":[subQ1,subQ3]});Q12=makeQuery(id+"F27.imprint","IMPRINT",FACE,{"disambiguationData":[TD([[makeQuery(id+"F27.imprint","IMPRINT",EDGE,{"disambiguationData":[TD([[subQ4,1.0]])],"derivedFrom":subQ3}),1.0]])]});}
            var Q13;
            {var subQ0=sQuery(id+"F27.wireOp",EDGE,"E28.filletArc");var subQ3=sQuery(id+"F27.wireOp",EDGE,"E36");var subQ5=makeQuery(id+"F27.imprint","INTERSECT",VERTEX,{"derivedFrom":[subQ0,subQ3]});Q13=makeQuery(id+"F27.imprint","IMPRINT",FACE,{"disambiguationData":[TD([[makeQuery(id+"F27.imprint","IMPRINT",EDGE,{"disambiguationData":[TD([[subQ5,-1.0]])],"derivedFrom":subQ3}),1.0]])]});}
            var Q14;
            {var subQ0=sQuery(id+"F27.wireOp",EDGE,"E28.filletArc");var subQ1=sQuery(id+"F27.wireOp",EDGE,"E27");var subQ2=makeQuery(id+"F27.imprint","INTERSECT",VERTEX,{"derivedFrom":[subQ1,subQ0]});Q14=makeQuery(id+"F27.imprint","IMPRINT",FACE,{"disambiguationData":[TD([[makeQuery(id+"F27.imprint","IMPRINT",EDGE,{"disambiguationData":[TD([[subQ2,-1.0]])],"derivedFrom":subQ1}),-1.0]])]});}
            var Q15;
            {var subQ0=sQuery(id+"F27.wireOp",EDGE,"E28.filletArc");var subQ1=sQuery(id+"F27.wireOp",EDGE,"E27");var subQ2=makeQuery(id+"F27.imprint","INTERSECT",VERTEX,{"derivedFrom":[subQ1,subQ0]});Q15=makeQuery(id+"F27.imprint","IMPRINT",FACE,{"disambiguationData":[TD([[makeQuery(id+"F27.imprint","IMPRINT",EDGE,{"disambiguationData":[TD([[subQ2,-1.0]])],"derivedFrom":subQ1}),1.0]])]});}
            var Q16;
            {var subQ0=sQuery(id+"F27.wireOp",EDGE,"E40.filletArc");Q16=makeQuery(id+"F27.imprint","IMPRINT",FACE,{"disambiguationData":[TD([[makeQuery(id+"F27.imprint","IMPRINT",EDGE,{"derivedFrom":subQ0}),-1.0]])]});}
            var Q17;
            {var subQ0=sQuery(id+"F27.wireOp",EDGE,"E40.filletArc");Q17=makeQuery(id+"F27.imprint","IMPRINT",FACE,{"disambiguationData":[TD([[makeQuery(id+"F27.imprint","IMPRINT",EDGE,{"derivedFrom":subQ0}),1.0]])]});}
            var Q18;
            {var subQ0=sQuery(id+"F27.wireOp",EDGE,"E39");var subQ1=sQuery(id+"F27.wireOp",EDGE,"E22.0");var subQ2=makeQuery(id+"F27.imprint","INTERSECT",VERTEX,{"disambiguationData":[OD(0.0)],"derivedFrom":[subQ1,subQ0]});Q18=makeQuery(id+"F27.imprint","IMPRINT",FACE,{"disambiguationData":[TD([[makeQuery(id+"F27.imprint","IMPRINT",EDGE,{"disambiguationData":[TD([[subQ2,-1.0]])],"derivedFrom":subQ1}),1.0]])]});}
            var Q19;
            {var subQ0=sQuery(id+"F27.wireOp",EDGE,"E39");var subQ1=sQuery(id+"F27.wireOp",EDGE,"E22.0");var subQ2=makeQuery(id+"F27.imprint","INTERSECT",VERTEX,{"disambiguationData":[OD(0.0)],"derivedFrom":[subQ1,subQ0]});Q19=makeQuery(id+"F27.imprint","IMPRINT",FACE,{"disambiguationData":[TD([[makeQuery(id+"F27.imprint","IMPRINT",EDGE,{"disambiguationData":[TD([[subQ2,-1.0]])],"derivedFrom":subQ1}),-1.0]])]});}
            var Q20;
            Q20=makeQuery(id+"F27.imprint","IMPRINT",FACE,{"disambiguationData":[TD([[makeQuery(id+"F27.imprint","IMPRINT",EDGE,{"derivedFrom":sQuery(id+"F27.wireOp",EDGE,"E18")}),1.0]])]});
            var Q21;
            {var subQ0=sQuery(id+"F27.wireOp",EDGE,"E41.filletArc");Q21=makeQuery(id+"F27.imprint","IMPRINT",FACE,{"disambiguationData":[TD([[makeQuery(id+"F27.imprint","IMPRINT",EDGE,{"derivedFrom":subQ0}),1.0]])]});}
            var Q22;
            {var subQ1=sQuery(id+"F27.wireOp",EDGE,"E19.0");var subQ3=sQuery(id+"F27.wireOp",EDGE,"E21");var subQ4=makeQuery(id+"F27.imprint","INTERSECT",VERTEX,{"derivedFrom":[subQ1,subQ3]});Q22=makeQuery(id+"F27.imprint","IMPRINT",FACE,{"disambiguationData":[TD([[makeQuery(id+"F27.imprint","IMPRINT",EDGE,{"disambiguationData":[TD([[subQ4,-1.0]])],"derivedFrom":subQ3}),1.0]])]});}
            var Q23;
            {var subQ0=sQuery(id+"F27.wireOp",EDGE,"E41.filletArc");Q23=makeQuery(id+"F27.imprint","IMPRINT",FACE,{"disambiguationData":[TD([[makeQuery(id+"F27.imprint","IMPRINT",EDGE,{"derivedFrom":subQ0}),-1.0]])]});}
            var Q24;
            Q24=sQuery(id+"F27.wireOp",EDGE,"E24");
            revolve(context, id + "F31", {"entities" : qUnion([Q0, Q1, Q2, Q3, Q4, Q5, Q6, Q7, Q8, Q9, Q10, Q11, Q12, Q13, Q14, Q15, Q16, Q17, Q18, Q19, Q20, Q21, Q22, Q23]), "axis" : qUnion([Q24]), "revolveType" : RevolveType.FULL});
        }
        {
            var Q0;
            Q0=makeQuery(id+"F29.opSweep","SWEPT_BODY",BODY,{"disambiguationData":[OSD([sQuery(id+"F27.wireOp",EDGE,"E22.0"),sQuery(id+"F28.wireOp",EDGE,"E44")])]});
            var Q1;
            Q1=sQuery(id+"F27.wireOp",EDGE,"E24");
            circularPattern(context, id + "F32", {"entities" : qUnion([Q0]), "axis" : qUnion([Q1]), "angle" : 360 * degree, "instanceCount" : 5, "equalSpace" : true});
        }
    });
